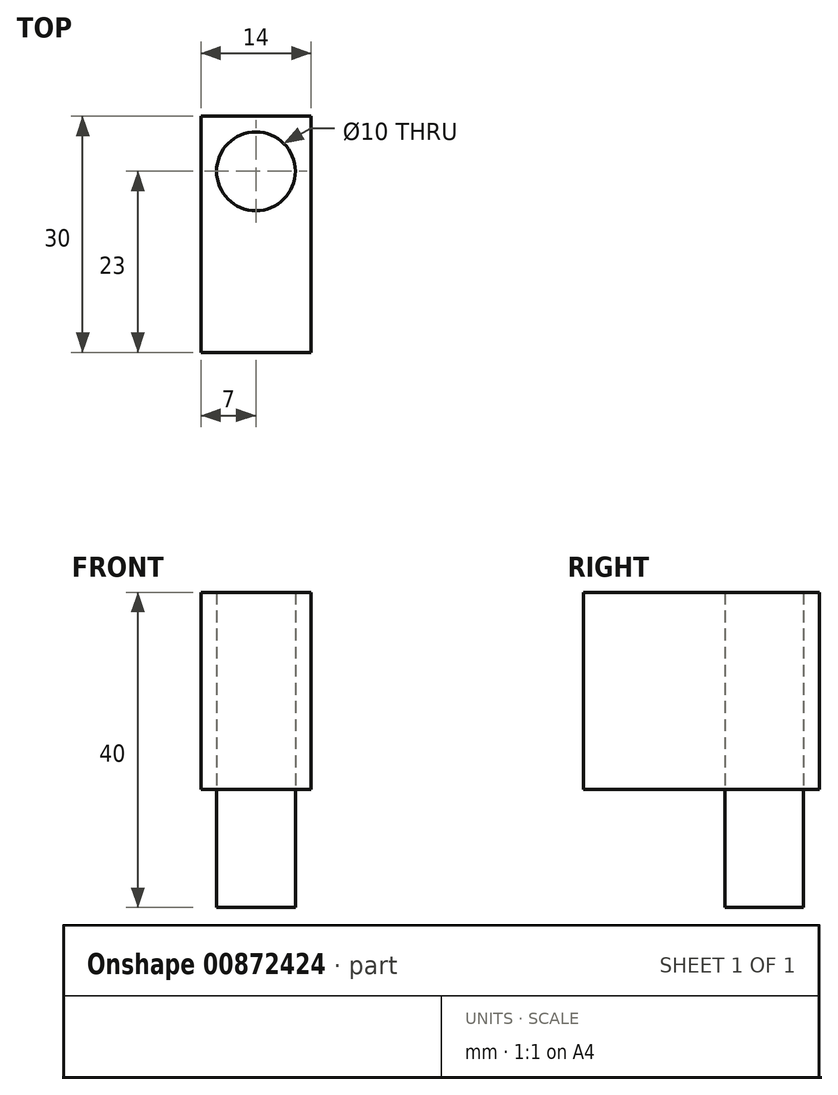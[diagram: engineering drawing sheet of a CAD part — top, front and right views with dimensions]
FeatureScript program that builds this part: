
annotation { "Feature Type Name" : "Feature", "Feature Type Description" : "" }
export const myFeature = defineFeature(function(context is Context, id is Id, definition is map)
    precondition{}
    {
        {
            var Q0;
            Q0=qCreatedBy(makeId("Top.planeOp"),FACE);
            var sketch = newSketch(context, id + "F0", { "sketchPlane" : qUnion([Q0])});
            skCircle(sketch, "E0", {"center": v(0, 0) * mm, "radius": 5 * mm});
            skSolve(sketch);
        }
        {
            var Q0;
            Q0=makeQuery(id+"F0.imprint","IMPRINT",FACE,{"disambiguationData":[TD([[makeQuery(id+"F0.imprint","IMPRINT",EDGE,{"derivedFrom":sQuery(id+"F0.wireOp",EDGE,"E0")}),1.0]])]});
            extrude(context, id + "F1", {"entities" : qUnion([Q0]), "depth" : 15 * mm, "offsetDistance" : 25 * mm});
        }
        {
            var Q0;
            Q0=makeQuery(id+"F1.opExtrude","CAP_FACE",FACE,{"disambiguationData":[OSD([sQuery(id+"F0.wireOp",EDGE,"E0")])],"isStart":false});
            var sketch = newSketch(context, id + "F2", { "sketchPlane" : qUnion([Q0])});
            skSolve(sketch);
        }
        {
            var Q0;
            Q0=makeQuery(id+"F2.imprint","IMPRINT",FACE,{"disambiguationData":[TD([[makeQuery(id+"F2.imprint","IMPRINT",EDGE,{"derivedFrom":makeQuery(id+"F1.opExtrude","CAP_EDGE",EDGE,{"disambiguationData":[OSD([sQuery(id+"F0.wireOp",EDGE,"E0")])],"isStart":false})}),1.0]])]});
            var sketch = newSketch(context, id + "F3", { "sketchPlane" : qUnion([Q0])});
            skLineSegment(sketch, "E1", {"start": v(0, 0) * mm, "end": v(0, 7) * mm});
            skLineSegment(sketch, "E2", {"start": v(0, 7) * mm, "end": v(7, 7) * mm});
            skLineSegment(sketch, "E3", {"start": v(0, 7) * mm, "end": v(-7, 7) * mm});
            skLineSegment(sketch, "E4", {"start": v(-7, 7) * mm, "end": v(-7, -23) * mm});
            skLineSegment(sketch, "E5", {"start": v(-7, -23) * mm, "end": v(7, -23) * mm});
            skLineSegment(sketch, "E6", {"start": v(7, -23) * mm, "end": v(7, 7) * mm});
            skSolve(sketch);
        }
        {
            var Q0;
            Q0=makeQuery(id+"F3.imprint","IMPRINT",FACE,{"disambiguationData":[TD([[makeQuery(id+"F3.imprint","IMPRINT",EDGE,{"derivedFrom":sQuery(id+"F3.wireOp",EDGE,"E2")}),-1.0]])]});
            extrude(context, id + "F4", {"entities" : qUnion([Q0]), "depth" : 25 * mm, "offsetDistance" : 25 * mm});
        }
        {
            var Q0;
            Q0=makeQuery(id+"F2.imprint","IMPRINT",FACE,{"disambiguationData":[TD([[makeQuery(id+"F2.imprint","IMPRINT",EDGE,{"derivedFrom":makeQuery(id+"F1.opExtrude","CAP_EDGE",EDGE,{"disambiguationData":[OSD([sQuery(id+"F0.wireOp",EDGE,"E0")])],"isStart":false})}),1.0]])]});
            extrude(context, id + "F5", {"entities" : qUnion([Q0]), "depth" : 25 * mm, "offsetDistance" : 25 * mm});
        }
    });
